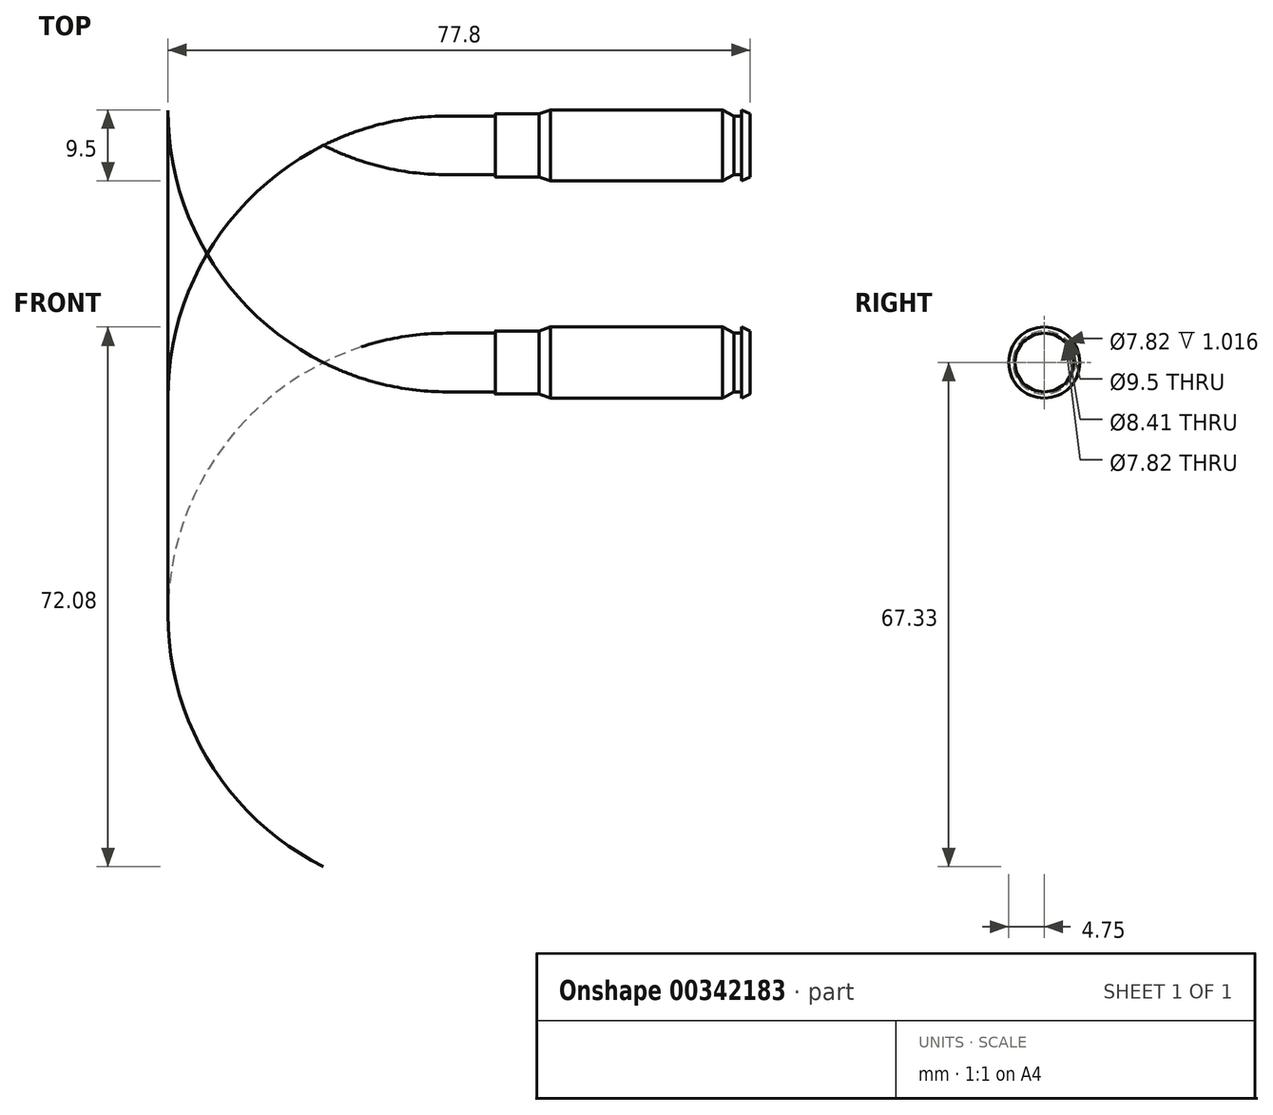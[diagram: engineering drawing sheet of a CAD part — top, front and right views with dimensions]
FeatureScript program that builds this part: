
annotation { "Feature Type Name" : "Feature", "Feature Type Description" : "" }
export const myFeature = defineFeature(function(context is Context, id is Id, definition is map)
    precondition{}
    {
        {
            var Q0;
            Q0=qCreatedBy(makeId("Top.planeOp"),FACE);
            var sketch = newSketch(context, id + "F0", { "sketchPlane" : qUnion([Q0])});
            skLineSegment(sketch, "E0", {"start": v(0, 0) * mm, "end": v(-70.17, 0) * mm, "construction": true});
            skLineSegment(sketch, "E1", {"start": v(0, 0) * mm, "end": v(0, 4.2) * mm});
            skLineSegment(sketch, "E2", {"start": v(0, 4.2) * mm, "end": v(-1.12, 4.75) * mm});
            skLineSegment(sketch, "E3", {"start": v(-1.12, 4.75) * mm, "end": v(-1.12, 3.91) * mm});
            skLineSegment(sketch, "E4", {"start": v(-1.12, 3.91) * mm, "end": v(-2.13, 3.91) * mm});
            skLineSegment(sketch, "E5", {"start": v(-2.13, 3.91) * mm, "end": v(-3.66, 4.75) * mm});
            skLineSegment(sketch, "E6", {"start": v(-3.66, 4.75) * mm, "end": v(-26.67, 4.75) * mm});
            skLineSegment(sketch, "E7", {"start": v(-28.17, 4.2) * mm, "end": v(-34.01, 4.2) * mm});
            skLineSegment(sketch, "E8", {"start": v(-34.06, 4.15) * mm, "end": v(-34.06, 3.96) * mm});
            skLineSegment(sketch, "E9", {"start": v(-34.11, 3.91) * mm, "end": v(-40.57, 3.91) * mm});
            skPoint(sketch, "E10.visualSharp", {"position": v(-34.06, 4.2) * mm});
            skArc(sketch, "E10.filletArc", {"start": v(-34.01, 4.2) * mm, "mid": v(-34.05, 4.19) * mm, "end": v(-34.06, 4.15) * mm});
            skPoint(sketch, "E11.visualSharp", {"position": v(-34.06, 3.91) * mm});
            skArc(sketch, "E11.filletArc", {"start": v(-34.11, 3.91) * mm, "mid": v(-34.08, 3.93) * mm, "end": v(-34.06, 3.96) * mm});
            skArc(sketch, "E12", {"start": v(-40.57, 3.91) * mm, "mid": v(-46.33, 3.45) * mm, "end": v(-51.94, 2.09) * mm});
            skArc(sketch, "E13", {"start": v(-51.94, 2.09) * mm, "mid": v(-54.5, 1.13) * mm, "end": v(-57, 0) * mm});
            skLineSegment(sketch, "E14", {"start": v(-28.17, 4.2) * mm, "end": v(-26.67, 4.75) * mm});
            skLineSegment(sketch, "E15", {"start": v(-57, 0) * mm, "end": v(0, 0) * mm});
            skSolve(sketch);
        }
        {
            var Q0;
            Q0 = qSketchRegion(id + "F0", true);
            var Q1;
            Q1=sQuery(id+"F0.wireOp",EDGE,"E0");
            revolve(context, id + "F1", {"entities" : qUnion([Q0]), "axis" : qUnion([Q1]), "revolveType" : RevolveType.FULL});
        }
    });
